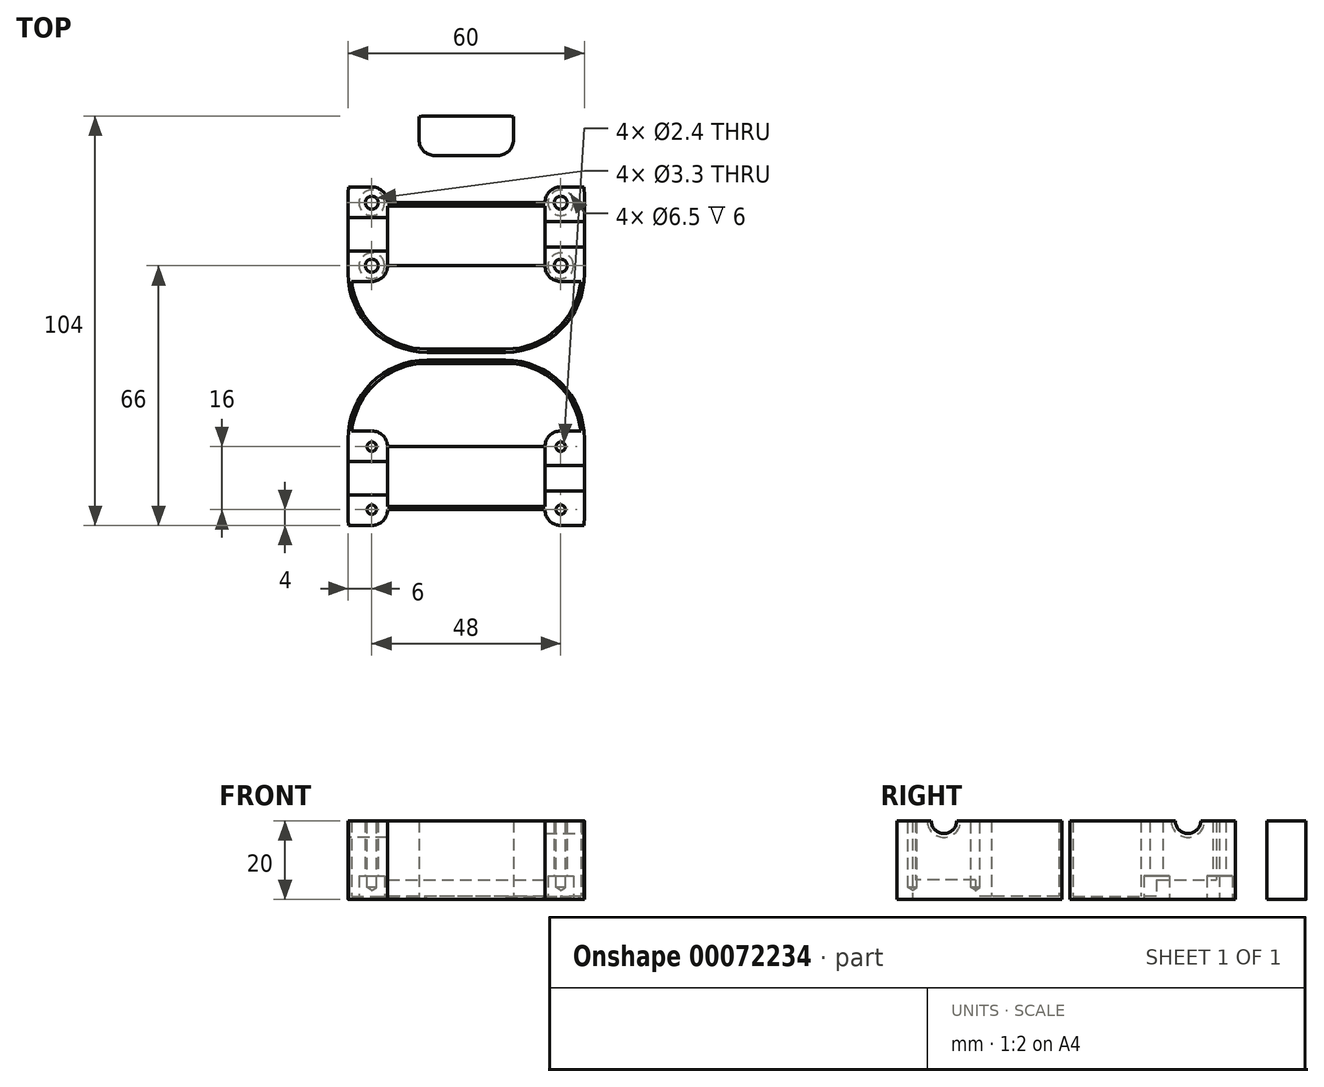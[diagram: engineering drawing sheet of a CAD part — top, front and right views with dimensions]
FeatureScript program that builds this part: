
annotation { "Feature Type Name" : "Feature", "Feature Type Description" : "" }
export const myFeature = defineFeature(function(context is Context, id is Id, definition is map)
    precondition{}
    {
        {
            var Q0;
            Q0=qCreatedBy(makeId("Top.planeOp"),FACE);
            var sketch = newSketch(context, id + "F0", { "sketchPlane" : qUnion([Q0])});
            skLineSegment(sketch, "E0", {"start": v(0, 0) * mm, "end": v(-30, 0) * mm, "construction": true});
            skLineSegment(sketch, "E1", {"start": v(0, 0) * mm, "end": v(0, 30) * mm, "construction": true});
            skLineSegment(sketch, "E2", {"start": v(0, 30) * mm, "end": v(-10, 30) * mm});
            skLineSegment(sketch, "E3", {"start": v(-30, 10) * mm, "end": v(-30, 0) * mm});
            skPoint(sketch, "E4.visualSharp", {"position": v(-30, 30) * mm});
            skArc(sketch, "E4.filletArc", {"start": v(-10, 30) * mm, "mid": v(-24.14, 24.14) * mm, "end": v(-30, 10) * mm});
            skArc(sketch, "E5.MirrorCS", {"start": v(10, 30) * mm, "mid": v(24.14, 24.14) * mm, "end": v(30, 10) * mm});
            skLineSegment(sketch, "E6.MirrorCS", {"start": v(30, 10) * mm, "end": v(30, 0) * mm});
            skLineSegment(sketch, "E7.MirrorCS", {"start": v(0, 30) * mm, "end": v(10, 30) * mm});
            skPoint(sketch, "E8.MirrorP", {"position": v(30, 30) * mm});
            skLineSegment(sketch, "E9.MirrorCS", {"start": v(0, -30) * mm, "end": v(-10, -30) * mm});
            skLineSegment(sketch, "E10.MirrorCS", {"start": v(-30, -10) * mm, "end": v(-30, 0) * mm});
            skLineSegment(sketch, "E11.MirrorCS", {"start": v(0, -30) * mm, "end": v(10, -30) * mm});
            skArc(sketch, "E12.MirrorCS", {"start": v(10, -30) * mm, "mid": v(24.14, -24.14) * mm, "end": v(30, -10) * mm});
            skArc(sketch, "E13.MirrorCS", {"start": v(-10, -30) * mm, "mid": v(-24.14, -24.14) * mm, "end": v(-30, -10) * mm});
            skLineSegment(sketch, "E14.MirrorCS", {"start": v(30, -10) * mm, "end": v(30, 0) * mm});
            skLineSegment(sketch, "E15.MirrorCS", {"start": v(0, 0) * mm, "end": v(0, -30) * mm, "construction": true});
            skPoint(sketch, "E16.MirrorP", {"position": v(30, -30) * mm});
            skPoint(sketch, "E17.MirrorP", {"position": v(-30, -30) * mm});
            skLineSegment(sketch, "E18", {"start": v(-16, 24) * mm, "end": v(0, 24) * mm, "construction": true});
            skLineSegment(sketch, "E19", {"start": v(-8, 30) * mm, "end": v(-8, 18.3) * mm, "construction": true});
            skPoint(sketch, "E19.startSnap0", {"position": v(-8, 24) * mm});
            skArc(sketch, "E20", {"start": v(-8, 20) * mm, "mid": v(-10.83, 21.17) * mm, "end": v(-12, 24) * mm});
            skLineSegment(sketch, "E21", {"start": v(-8, 20) * mm, "end": v(0, 20) * mm});
            skLineSegment(sketch, "E22", {"start": v(-24, 17.1) * mm, "end": v(-24, 0) * mm, "construction": true});
            skLineSegment(sketch, "E23", {"start": v(-30, 8) * mm, "end": v(-16.95, 8) * mm, "construction": true});
            skArc(sketch, "E24", {"start": v(-24, 12) * mm, "mid": v(-21.17, 10.83) * mm, "end": v(-20, 8) * mm});
            skLineSegment(sketch, "E25", {"start": v(-20, 8) * mm, "end": v(-20, 0) * mm});
            skLineSegment(sketch, "E26", {"start": v(-24, 12) * mm, "end": v(-36.57, 12) * mm});
            skLineSegment(sketch, "E27.MirrorCS", {"start": v(-24, -12) * mm, "end": v(-36.57, -12) * mm});
            skLineSegment(sketch, "E28.MirrorCS", {"start": v(-20, -8) * mm, "end": v(-20, 0) * mm});
            skArc(sketch, "E29.MirrorCS", {"start": v(-24, -12) * mm, "mid": v(-21.17, -10.83) * mm, "end": v(-20, -8) * mm});
            skLineSegment(sketch, "E30.MirrorCS", {"start": v(24, 12) * mm, "end": v(36.57, 12) * mm});
            skArc(sketch, "E31.MirrorCS", {"start": v(24, 12) * mm, "mid": v(21.17, 10.83) * mm, "end": v(20, 8) * mm});
            skLineSegment(sketch, "E32.MirrorCS", {"start": v(20, 8) * mm, "end": v(20, 0) * mm});
            skLineSegment(sketch, "E33.MirrorCS", {"start": v(24, -12) * mm, "end": v(36.57, -12) * mm});
            skLineSegment(sketch, "E34.MirrorCS", {"start": v(20, -8) * mm, "end": v(20, 0) * mm});
            skArc(sketch, "E35.MirrorCS", {"start": v(24, -12) * mm, "mid": v(21.17, -10.83) * mm, "end": v(20, -8) * mm});
            skLineSegment(sketch, "E36", {"start": v(-12, 24) * mm, "end": v(-12, 35.75) * mm});
            skLineSegment(sketch, "E37.MirrorCS", {"start": v(8, 20) * mm, "end": v(0, 20) * mm});
            skLineSegment(sketch, "E38.MirrorCS", {"start": v(12, 24) * mm, "end": v(12, 35.75) * mm});
            skArc(sketch, "E39.MirrorCS", {"start": v(8, 20) * mm, "mid": v(10.83, 21.17) * mm, "end": v(12, 24) * mm});
            skLineSegment(sketch, "E40.bottom", {"start": v(-20, -8) * mm, "end": v(20, -8) * mm});
            skLineSegment(sketch, "E40.top", {"start": v(-20, 8) * mm, "end": v(20, 8) * mm});
            skLineSegment(sketch, "E40.left", {"start": v(-20, -8) * mm, "end": v(-20, 8) * mm});
            skLineSegment(sketch, "E40.right", {"start": v(20, -8) * mm, "end": v(20, 8) * mm});
            skSolve(sketch);
        }
        {
            var Q0;
            {var subQ19=sQuery(id+"F0.wireOp",EDGE,"E9.MirrorCS");Q0=makeQuery(id+"F0.imprint","IMPRINT",FACE,{"disambiguationData":[TD([[makeQuery(id+"F0.imprint","IMPRINT",EDGE,{"derivedFrom":subQ19}),-1.0]])]});}
            var Q1;
            {var subQ6=sQuery(id+"F0.wireOp",EDGE,"E3");Q1=makeQuery(id+"F0.imprint","IMPRINT",FACE,{"disambiguationData":[TD([[makeQuery(id+"F0.imprint","IMPRINT",EDGE,{"derivedFrom":subQ6}),1.0]])]});}
            var Q2;
            {var subQ1=sQuery(id+"F0.wireOp",EDGE,"E6.MirrorCS");Q2=makeQuery(id+"F0.imprint","IMPRINT",FACE,{"disambiguationData":[TD([[makeQuery(id+"F0.imprint","IMPRINT",EDGE,{"derivedFrom":subQ1}),-1.0]])]});}
            var Q3;
            {var subQ1=sQuery(id+"F0.wireOp",EDGE,"E2");Q3=makeQuery(id+"F0.imprint","IMPRINT",FACE,{"disambiguationData":[TD([[makeQuery(id+"F0.imprint","IMPRINT",EDGE,{"derivedFrom":subQ1}),1.0]])]});}
            var Q4;
            {var subQ1=sQuery(id+"F0.wireOp",EDGE,"E20");Q4=makeQuery(id+"F0.imprint","IMPRINT",FACE,{"disambiguationData":[TD([[makeQuery(id+"F0.imprint","IMPRINT",EDGE,{"derivedFrom":subQ1}),1.0]])]});}
            var Q5;
            Q5=makeQuery(id+"F0.imprint","IMPRINT",FACE,{"disambiguationData":[TD([[makeQuery(id+"F0.imprint","IMPRINT",EDGE,{"derivedFrom":sQuery(id+"F0.wireOp",EDGE,"E40.bottom")}),1.0]])]});
            extrude(context, id + "F1", {"entities" : qUnion([Q0, Q1, Q2, Q3, Q4, Q5]), "depth" : 20 * mm, "offsetDistance" : 25 * mm});
        }
        {
            var Q0;
            Q0=makeQuery(id+"F1.opExtrude","CAP_FACE",FACE,{"disambiguationData":[OSD([sQuery(id+"F0.wireOp",EDGE,"E3"),sQuery(id+"F0.wireOp",EDGE,"E6.MirrorCS"),sQuery(id+"F0.wireOp",EDGE,"E4.filletArc"),sQuery(id+"F0.wireOp",EDGE,"E5.MirrorCS"),sQuery(id+"F0.wireOp",EDGE,"E2"),sQuery(id+"F0.wireOp",EDGE,"E7.MirrorCS"),sQuery(id+"F0.wireOp",EDGE,"E9.MirrorCS"),sQuery(id+"F0.wireOp",EDGE,"E12.MirrorCS"),sQuery(id+"F0.wireOp",EDGE,"E11.MirrorCS"),sQuery(id+"F0.wireOp",EDGE,"E10.MirrorCS"),sQuery(id+"F0.wireOp",EDGE,"E14.MirrorCS"),sQuery(id+"F0.wireOp",EDGE,"E13.MirrorCS")])],"isStart":false});
            shell(context, id + "F2", {"entities" : qUnion([Q0]), "thickness" : 0.8 * mm});
        }
        {
            var Q0;
            Q0=makeQuery(id+"F0.imprint","IMPRINT",FACE,{"disambiguationData":[TD([[makeQuery(id+"F0.imprint","IMPRINT",EDGE,{"derivedFrom":sQuery(id+"F0.wireOp",EDGE,"E40.bottom")}),1.0]])]});
            extrude(context, id + "F3", {"entities" : qUnion([Q0]), "operationType" : NewBodyOperationType.ADD, "depth" : 5 * mm, "offsetDistance" : 25 * mm});
        }
        {
            var Q0;
            {var subQ1=sQuery(id+"F0.wireOp",EDGE,"E14.MirrorCS");Q0=makeQuery(id+"F0.imprint","IMPRINT",FACE,{"disambiguationData":[TD([[makeQuery(id+"F0.imprint","IMPRINT",EDGE,{"derivedFrom":subQ1}),1.0]])]});}
            var Q1;
            {var subQ2=sQuery(id+"F0.wireOp",EDGE,"14543c69-8659-48dd-a31f-9fa6a3777b9e38.MirrorCS");Q1=makeQuery(id+"F0.imprint","IMPRINT",FACE,{"disambiguationData":[TD([[makeQuery(id+"F0.imprint","IMPRINT",EDGE,{"derivedFrom":subQ2}),-1.0]])]});}
            var Q2;
            Q2=makeQuery(id+"F0.imprint","IMPRINT",FACE,{"disambiguationData":[TD([[makeQuery(id+"F0.imprint","IMPRINT",EDGE,{"derivedFrom":sQuery(id+"F0.wireOp",EDGE,"E2")}),1.0]])]});
            var Q3;
            {var subQ3=sQuery(id+"F0.wireOp",EDGE,"E10.MirrorCS");Q3=makeQuery(id+"F0.imprint","IMPRINT",FACE,{"disambiguationData":[TD([[makeQuery(id+"F0.imprint","IMPRINT",EDGE,{"derivedFrom":subQ3}),-1.0]])]});}
            var Q4;
            {var subQ3=sQuery(id+"F0.wireOp",EDGE,"E3");Q4=makeQuery(id+"F0.imprint","IMPRINT",FACE,{"disambiguationData":[TD([[makeQuery(id+"F0.imprint","IMPRINT",EDGE,{"derivedFrom":subQ3}),1.0]])]});}
            var Q5;
            Q5=sQuery(id+"F0.wireOp",EDGE,"b274ORE4-UM5T-iyJz-Mf7x-KISBnKHlPYNR");
            extrude(context, id + "F4", {"entities" : qUnion([Q0, Q1, Q2, Q3, Q4]), "operationType" : NewBodyOperationType.ADD, "surfaceEntities" : qUnion([Q5]), "depth" : 20 * mm});
        }
        {
            var Q0;
            Q0=makeQuery(id+"F1.opExtrude","SWEPT_FACE",FACE,{"disambiguationData":[OSD([sQuery(id+"F0.wireOp",EDGE,"E3"),sQuery(id+"F0.wireOp",EDGE,"E10.MirrorCS"),sQuery(id+"F0.wireOp",EDGE,"e1145777-d645-4c14-8510-543826b77d7c3.MirrorCS"),sQuery(id+"F0.wireOp",EDGE,"e1145777-d645-4c14-8510-543826b77d7c7.MirrorCS")])]});
            var sketch = newSketch(context, id + "F5", { "sketchPlane" : qUnion([Q0])});
            skPoint(sketch, "E41", {"position": v(0, 20) * mm});
            skSolve(sketch);
        }
        {
            var Q0;
            Q0=sQuery(id+"F5.wireOp",VERTEX,"E41");
            var Q1;
            Q1=makeQuery(id+"F1.opExtrude","SWEPT_BODY",BODY,{"disambiguationData":[OSD([sQuery(id+"F0.wireOp",EDGE,"E3"),sQuery(id+"F0.wireOp",EDGE,"E6.MirrorCS"),sQuery(id+"F0.wireOp",EDGE,"E4.filletArc"),sQuery(id+"F0.wireOp",EDGE,"E5.MirrorCS"),sQuery(id+"F0.wireOp",EDGE,"E2"),sQuery(id+"F0.wireOp",EDGE,"E7.MirrorCS"),sQuery(id+"F0.wireOp",EDGE,"E9.MirrorCS"),sQuery(id+"F0.wireOp",EDGE,"E12.MirrorCS"),sQuery(id+"F0.wireOp",EDGE,"E11.MirrorCS"),sQuery(id+"F0.wireOp",EDGE,"E10.MirrorCS"),sQuery(id+"F0.wireOp",EDGE,"E14.MirrorCS"),sQuery(id+"F0.wireOp",EDGE,"E13.MirrorCS"),sQuery(id+"F0.wireOp",EDGE,"b274ORE4-UM5T-iyJz-Mf7x-KISBnKHlPYNR"),sQuery(id+"F0.wireOp",EDGE,"e1145777-d645-4c14-8510-543826b77d7c3.MirrorCS"),sQuery(id+"F0.wireOp",EDGE,"e1145777-d645-4c14-8510-543826b77d7c7.MirrorCS"),sQuery(id+"F0.wireOp",EDGE,"d4da72d8-b042-4007-9413-fc62ccedf90810.MirrorCS"),sQuery(id+"F0.wireOp",EDGE,"d4da72d8-b042-4007-9413-fc62ccedf90813.MirrorCS"),sQuery(id+"F0.wireOp",EDGE,"A0MarJfp-02qR-F9tc-DTzI-DnbxqoHxPLbg.bottom"),sQuery(id+"F0.wireOp",EDGE,"92cf4c97-c3a1-482c-a76c-706df4ada76c3.MirrorCS")])]});
            var Q2;
            Q2=makeQuery(id+"FBtsKpCSnu7iRzL_1.opExtrude","SWEPT_BODY",BODY,{"disambiguationData":[OSD([sQuery(id+"F0.wireOp",EDGE,"E3"),sQuery(id+"F0.wireOp",EDGE,"E6.MirrorCS"),sQuery(id+"F0.wireOp",EDGE,"E4.filletArc"),sQuery(id+"F0.wireOp",EDGE,"E5.MirrorCS"),sQuery(id+"F0.wireOp",EDGE,"E2"),sQuery(id+"F0.wireOp",EDGE,"E7.MirrorCS"),sQuery(id+"F0.wireOp",EDGE,"E9.MirrorCS"),sQuery(id+"F0.wireOp",EDGE,"E12.MirrorCS"),sQuery(id+"F0.wireOp",EDGE,"E11.MirrorCS"),sQuery(id+"F0.wireOp",EDGE,"E10.MirrorCS"),sQuery(id+"F0.wireOp",EDGE,"E14.MirrorCS"),sQuery(id+"F0.wireOp",EDGE,"E13.MirrorCS"),sQuery(id+"F0.wireOp",EDGE,"b274ORE4-UM5T-iyJz-Mf7x-KISBnKHlPYNR"),sQuery(id+"F0.wireOp",EDGE,"e1145777-d645-4c14-8510-543826b77d7c3.MirrorCS"),sQuery(id+"F0.wireOp",EDGE,"e1145777-d645-4c14-8510-543826b77d7c7.MirrorCS"),sQuery(id+"F0.wireOp",EDGE,"d4da72d8-b042-4007-9413-fc62ccedf90810.MirrorCS"),sQuery(id+"F0.wireOp",EDGE,"d4da72d8-b042-4007-9413-fc62ccedf90813.MirrorCS"),sQuery(id+"F0.wireOp",EDGE,"A0MarJfp-02qR-F9tc-DTzI-DnbxqoHxPLbg.bottom"),sQuery(id+"F0.wireOp",EDGE,"92cf4c97-c3a1-482c-a76c-706df4ada76c3.MirrorCS")])]});
            hole(context, id + "F6", {"style" : HoleStyle.SIMPLE, "endStyle" : HoleEndStyle.BLIND, "holeDiameter" : 8.5 * mm, "holeDepth" : 12 * mm, "locations" : qUnion([Q0]), "scope" : qUnion([Q1, Q2])});
        }
        {
            var Q0;
            Q0=makeQuery(id+"F1.opExtrude","SWEPT_FACE",FACE,{"disambiguationData":[OSD([sQuery(id+"F0.wireOp",EDGE,"E2"),sQuery(id+"F0.wireOp",EDGE,"E7.MirrorCS"),sQuery(id+"F0.wireOp",EDGE,"A0MarJfp-02qR-F9tc-DTzI-DnbxqoHxPLbg.bottom"),sQuery(id+"F0.wireOp",EDGE,"92cf4c97-c3a1-482c-a76c-706df4ada76c3.MirrorCS")])]});
            var sketch = newSketch(context, id + "F7", { "sketchPlane" : qUnion([Q0])});
            skPoint(sketch, "E42", {"position": v(0, 20) * mm});
            skSolve(sketch);
        }
        {
            var Q0;
            Q0=sQuery(id+"F7.wireOp",VERTEX,"E42");
            var Q1;
            Q1=makeQuery(id+"F1.opExtrude","SWEPT_BODY",BODY,{"disambiguationData":[OSD([sQuery(id+"F0.wireOp",EDGE,"E3"),sQuery(id+"F0.wireOp",EDGE,"E6.MirrorCS"),sQuery(id+"F0.wireOp",EDGE,"E4.filletArc"),sQuery(id+"F0.wireOp",EDGE,"E5.MirrorCS"),sQuery(id+"F0.wireOp",EDGE,"E2"),sQuery(id+"F0.wireOp",EDGE,"E7.MirrorCS"),sQuery(id+"F0.wireOp",EDGE,"E9.MirrorCS"),sQuery(id+"F0.wireOp",EDGE,"E12.MirrorCS"),sQuery(id+"F0.wireOp",EDGE,"E11.MirrorCS"),sQuery(id+"F0.wireOp",EDGE,"E10.MirrorCS"),sQuery(id+"F0.wireOp",EDGE,"E14.MirrorCS"),sQuery(id+"F0.wireOp",EDGE,"E13.MirrorCS"),sQuery(id+"F0.wireOp",EDGE,"b274ORE4-UM5T-iyJz-Mf7x-KISBnKHlPYNR"),sQuery(id+"F0.wireOp",EDGE,"e1145777-d645-4c14-8510-543826b77d7c3.MirrorCS"),sQuery(id+"F0.wireOp",EDGE,"e1145777-d645-4c14-8510-543826b77d7c7.MirrorCS"),sQuery(id+"F0.wireOp",EDGE,"d4da72d8-b042-4007-9413-fc62ccedf90810.MirrorCS"),sQuery(id+"F0.wireOp",EDGE,"d4da72d8-b042-4007-9413-fc62ccedf90813.MirrorCS"),sQuery(id+"F0.wireOp",EDGE,"A0MarJfp-02qR-F9tc-DTzI-DnbxqoHxPLbg.bottom"),sQuery(id+"F0.wireOp",EDGE,"92cf4c97-c3a1-482c-a76c-706df4ada76c3.MirrorCS")])]});
            hole(context, id + "F8", {"style" : HoleStyle.SIMPLE, "endStyle" : HoleEndStyle.BLIND, "holeDiameter" : 8.5 * mm, "holeDepth" : 12 * mm, "locations" : qUnion([Q0]), "scope" : qUnion([Q1])});
        }
        {
            var Q0;
            Q0=makeQuery(id+"F1.opExtrude","SWEPT_FACE",FACE,{"disambiguationData":[OSD([sQuery(id+"F0.wireOp",EDGE,"E6.MirrorCS"),sQuery(id+"F0.wireOp",EDGE,"E14.MirrorCS")])]});
            var sketch = newSketch(context, id + "F9", { "sketchPlane" : qUnion([Q0])});
            skPoint(sketch, "E43", {"position": v(0, 20) * mm});
            skSolve(sketch);
        }
        {
            var Q0;
            Q0=sQuery(id+"F9.wireOp",VERTEX,"E43");
            var Q1;
            Q1=makeQuery(id+"F1.opExtrude","SWEPT_BODY",BODY,{"disambiguationData":[OSD([sQuery(id+"F0.wireOp",EDGE,"E3"),sQuery(id+"F0.wireOp",EDGE,"E6.MirrorCS"),sQuery(id+"F0.wireOp",EDGE,"E4.filletArc"),sQuery(id+"F0.wireOp",EDGE,"E5.MirrorCS"),sQuery(id+"F0.wireOp",EDGE,"E2"),sQuery(id+"F0.wireOp",EDGE,"E7.MirrorCS"),sQuery(id+"F0.wireOp",EDGE,"E9.MirrorCS"),sQuery(id+"F0.wireOp",EDGE,"E12.MirrorCS"),sQuery(id+"F0.wireOp",EDGE,"E11.MirrorCS"),sQuery(id+"F0.wireOp",EDGE,"E10.MirrorCS"),sQuery(id+"F0.wireOp",EDGE,"E14.MirrorCS"),sQuery(id+"F0.wireOp",EDGE,"E13.MirrorCS"),sQuery(id+"F0.wireOp",EDGE,"b274ORE4-UM5T-iyJz-Mf7x-KISBnKHlPYNR"),sQuery(id+"F0.wireOp",EDGE,"e1145777-d645-4c14-8510-543826b77d7c3.MirrorCS"),sQuery(id+"F0.wireOp",EDGE,"e1145777-d645-4c14-8510-543826b77d7c7.MirrorCS"),sQuery(id+"F0.wireOp",EDGE,"d4da72d8-b042-4007-9413-fc62ccedf90810.MirrorCS"),sQuery(id+"F0.wireOp",EDGE,"d4da72d8-b042-4007-9413-fc62ccedf90813.MirrorCS"),sQuery(id+"F0.wireOp",EDGE,"A0MarJfp-02qR-F9tc-DTzI-DnbxqoHxPLbg.bottom"),sQuery(id+"F0.wireOp",EDGE,"92cf4c97-c3a1-482c-a76c-706df4ada76c3.MirrorCS")])]});
            var Q2;
            Q2=makeQuery(id+"FBtsKpCSnu7iRzL_1.opExtrude","SWEPT_BODY",BODY,{"disambiguationData":[OSD([sQuery(id+"F0.wireOp",EDGE,"E3"),sQuery(id+"F0.wireOp",EDGE,"E6.MirrorCS"),sQuery(id+"F0.wireOp",EDGE,"E4.filletArc"),sQuery(id+"F0.wireOp",EDGE,"E5.MirrorCS"),sQuery(id+"F0.wireOp",EDGE,"E2"),sQuery(id+"F0.wireOp",EDGE,"E7.MirrorCS"),sQuery(id+"F0.wireOp",EDGE,"E9.MirrorCS"),sQuery(id+"F0.wireOp",EDGE,"E12.MirrorCS"),sQuery(id+"F0.wireOp",EDGE,"E11.MirrorCS"),sQuery(id+"F0.wireOp",EDGE,"E10.MirrorCS"),sQuery(id+"F0.wireOp",EDGE,"E14.MirrorCS"),sQuery(id+"F0.wireOp",EDGE,"E13.MirrorCS"),sQuery(id+"F0.wireOp",EDGE,"b274ORE4-UM5T-iyJz-Mf7x-KISBnKHlPYNR"),sQuery(id+"F0.wireOp",EDGE,"e1145777-d645-4c14-8510-543826b77d7c3.MirrorCS"),sQuery(id+"F0.wireOp",EDGE,"e1145777-d645-4c14-8510-543826b77d7c7.MirrorCS"),sQuery(id+"F0.wireOp",EDGE,"d4da72d8-b042-4007-9413-fc62ccedf90810.MirrorCS"),sQuery(id+"F0.wireOp",EDGE,"d4da72d8-b042-4007-9413-fc62ccedf90813.MirrorCS"),sQuery(id+"F0.wireOp",EDGE,"A0MarJfp-02qR-F9tc-DTzI-DnbxqoHxPLbg.bottom"),sQuery(id+"F0.wireOp",EDGE,"92cf4c97-c3a1-482c-a76c-706df4ada76c3.MirrorCS")])]});
            hole(context, id + "F10", {"style" : HoleStyle.SIMPLE, "endStyle" : HoleEndStyle.BLIND, "holeDiameter" : 6.5 * mm, "holeDepth" : 12 * mm, "locations" : qUnion([Q0]), "scope" : qUnion([Q1, Q2])});
        }
        {
            var Q0;
            Q0=qCreatedBy(makeId("Front.planeOp"),FACE);
            cPlane(context, id + "F11", {"entities" : qUnion([Q0]), "cplaneType" : CPlaneType.OFFSET, "offset" : 31 * mm, "width" : 150 * mm, "height" : 150 * mm});
        }
        {
            var Q0;
            Q0=makeQuery(id+"F1.opExtrude","SWEPT_BODY",BODY,{"disambiguationData":[OSD([sQuery(id+"F0.wireOp",EDGE,"E3"),sQuery(id+"F0.wireOp",EDGE,"E6.MirrorCS"),sQuery(id+"F0.wireOp",EDGE,"E4.filletArc"),sQuery(id+"F0.wireOp",EDGE,"E5.MirrorCS"),sQuery(id+"F0.wireOp",EDGE,"E2"),sQuery(id+"F0.wireOp",EDGE,"E7.MirrorCS"),sQuery(id+"F0.wireOp",EDGE,"E9.MirrorCS"),sQuery(id+"F0.wireOp",EDGE,"E12.MirrorCS"),sQuery(id+"F0.wireOp",EDGE,"E11.MirrorCS"),sQuery(id+"F0.wireOp",EDGE,"E10.MirrorCS"),sQuery(id+"F0.wireOp",EDGE,"E14.MirrorCS"),sQuery(id+"F0.wireOp",EDGE,"E13.MirrorCS"),sQuery(id+"F0.wireOp",EDGE,"b274ORE4-UM5T-iyJz-Mf7x-KISBnKHlPYNR"),sQuery(id+"F0.wireOp",EDGE,"e1145777-d645-4c14-8510-543826b77d7c3.MirrorCS"),sQuery(id+"F0.wireOp",EDGE,"e1145777-d645-4c14-8510-543826b77d7c7.MirrorCS"),sQuery(id+"F0.wireOp",EDGE,"d4da72d8-b042-4007-9413-fc62ccedf90810.MirrorCS"),sQuery(id+"F0.wireOp",EDGE,"d4da72d8-b042-4007-9413-fc62ccedf90813.MirrorCS"),sQuery(id+"F0.wireOp",EDGE,"A0MarJfp-02qR-F9tc-DTzI-DnbxqoHxPLbg.bottom"),sQuery(id+"F0.wireOp",EDGE,"92cf4c97-c3a1-482c-a76c-706df4ada76c3.MirrorCS")])]});
            var Q1;
            Q1=qCreatedBy(id+"F11.planeOp",FACE);
            mirror(context, id + "F12", {"entities" : qUnion([Q0]), "mirrorPlane" : qUnion([Q1])});
        }
        {
            var Q0;
            Q0=sQuery(id+"F0.wireOp",VERTEX,"E24.center");
            var Q1;
            Q1=sQuery(id+"F0.wireOp",VERTEX,"E31.MirrorCS.center");
            var Q2;
            Q2=sQuery(id+"F0.wireOp",VERTEX,"E35.MirrorCS.center");
            var Q3;
            Q3=sQuery(id+"F0.wireOp",VERTEX,"E29.MirrorCS.center");
            var Q4;
            Q4=makeQuery(id+"F1.opExtrude","SWEPT_BODY",BODY,{"disambiguationData":[OSD([sQuery(id+"F0.wireOp",EDGE,"E3"),sQuery(id+"F0.wireOp",EDGE,"E6.MirrorCS"),sQuery(id+"F0.wireOp",EDGE,"E4.filletArc"),sQuery(id+"F0.wireOp",EDGE,"E5.MirrorCS"),sQuery(id+"F0.wireOp",EDGE,"E2"),sQuery(id+"F0.wireOp",EDGE,"E7.MirrorCS"),sQuery(id+"F0.wireOp",EDGE,"E9.MirrorCS"),sQuery(id+"F0.wireOp",EDGE,"E12.MirrorCS"),sQuery(id+"F0.wireOp",EDGE,"E11.MirrorCS"),sQuery(id+"F0.wireOp",EDGE,"E10.MirrorCS"),sQuery(id+"F0.wireOp",EDGE,"E14.MirrorCS"),sQuery(id+"F0.wireOp",EDGE,"E13.MirrorCS"),sQuery(id+"F0.wireOp",EDGE,"b274ORE4-UM5T-iyJz-Mf7x-KISBnKHlPYNR"),sQuery(id+"F0.wireOp",EDGE,"e1145777-d645-4c14-8510-543826b77d7c3.MirrorCS"),sQuery(id+"F0.wireOp",EDGE,"e1145777-d645-4c14-8510-543826b77d7c7.MirrorCS"),sQuery(id+"F0.wireOp",EDGE,"d4da72d8-b042-4007-9413-fc62ccedf90810.MirrorCS"),sQuery(id+"F0.wireOp",EDGE,"d4da72d8-b042-4007-9413-fc62ccedf90813.MirrorCS"),sQuery(id+"F0.wireOp",EDGE,"A0MarJfp-02qR-F9tc-DTzI-DnbxqoHxPLbg.bottom"),sQuery(id+"F0.wireOp",EDGE,"92cf4c97-c3a1-482c-a76c-706df4ada76c3.MirrorCS")])]});
            var Q5;
            Q5=makeQuery(id+"F12.opPattern","COPY",BODY,{"derivedFrom":makeQuery(id+"F1.opExtrude","SWEPT_BODY",BODY,{"disambiguationData":[OSD([sQuery(id+"F0.wireOp",EDGE,"E3"),sQuery(id+"F0.wireOp",EDGE,"E6.MirrorCS"),sQuery(id+"F0.wireOp",EDGE,"E4.filletArc"),sQuery(id+"F0.wireOp",EDGE,"E5.MirrorCS"),sQuery(id+"F0.wireOp",EDGE,"E2"),sQuery(id+"F0.wireOp",EDGE,"E7.MirrorCS"),sQuery(id+"F0.wireOp",EDGE,"E9.MirrorCS"),sQuery(id+"F0.wireOp",EDGE,"E12.MirrorCS"),sQuery(id+"F0.wireOp",EDGE,"E11.MirrorCS"),sQuery(id+"F0.wireOp",EDGE,"E10.MirrorCS"),sQuery(id+"F0.wireOp",EDGE,"E14.MirrorCS"),sQuery(id+"F0.wireOp",EDGE,"E13.MirrorCS"),sQuery(id+"F0.wireOp",EDGE,"b274ORE4-UM5T-iyJz-Mf7x-KISBnKHlPYNR"),sQuery(id+"F0.wireOp",EDGE,"e1145777-d645-4c14-8510-543826b77d7c3.MirrorCS"),sQuery(id+"F0.wireOp",EDGE,"e1145777-d645-4c14-8510-543826b77d7c7.MirrorCS"),sQuery(id+"F0.wireOp",EDGE,"d4da72d8-b042-4007-9413-fc62ccedf90810.MirrorCS"),sQuery(id+"F0.wireOp",EDGE,"d4da72d8-b042-4007-9413-fc62ccedf90813.MirrorCS"),sQuery(id+"F0.wireOp",EDGE,"A0MarJfp-02qR-F9tc-DTzI-DnbxqoHxPLbg.bottom"),sQuery(id+"F0.wireOp",EDGE,"92cf4c97-c3a1-482c-a76c-706df4ada76c3.MirrorCS")])]}),"instanceName":"1"});
            hole(context, id + "F13", {"style" : HoleStyle.C_BORE, "endStyle" : HoleEndStyle.THROUGH, "oppositeDirection" : true, "holeDiameter" : 3.3 * mm, "cBoreDiameter" : 6.5 * mm, "cBoreDepth" : 6 * mm, "locations" : qUnion([Q0, Q1, Q2, Q3]), "scope" : qUnion([Q4, Q5]), "isTappedThrough" : true});
        }
        {
            var Q0;
            {var subQ0=sQuery(id+"F0.wireOp",EDGE,"E26");var subQ1=sQuery(id+"F0.wireOp",EDGE,"E28.MirrorCS");var subQ2=sQuery(id+"F0.wireOp",EDGE,"E25");var subQ3=sQuery(id+"F0.wireOp",EDGE,"E10.MirrorCS");var subQ4=sQuery(id+"F0.wireOp",EDGE,"E3");var subQ5=sQuery(id+"F0.wireOp",EDGE,"E24");var subQ6=sQuery(id+"F0.wireOp",EDGE,"E37.MirrorCS");var subQ7=sQuery(id+"F0.wireOp",EDGE,"E21");var subQ8=sQuery(id+"F0.wireOp",EDGE,"E20");var subQ9=sQuery(id+"F0.wireOp",EDGE,"E4.filletArc");var subQ10=sQuery(id+"F0.wireOp",EDGE,"E36");var subQ11=sQuery(id+"F0.wireOp",EDGE,"E7.MirrorCS");var subQ12=sQuery(id+"F0.wireOp",EDGE,"E2");var subQ13=sQuery(id+"F0.wireOp",EDGE,"E14.MirrorCS");var subQ14=sQuery(id+"F0.wireOp",EDGE,"E6.MirrorCS");var subQ15=sQuery(id+"F0.wireOp",EDGE,"E12.MirrorCS");var subQ16=sQuery(id+"F0.wireOp",EDGE,"E5.MirrorCS");var subQ17=sQuery(id+"F0.wireOp",EDGE,"E13.MirrorCS");Q0=makeQuery(id+"F12.opPattern","COPY",FACE,{"derivedFrom":makeQuery(id+"F8.hole-0.boolean.opBoolean","SPLIT",FACE,{"disambiguationData":[TD([makeQuery(id+"F1.opExtrude","SWEPT_FACE",FACE,{"disambiguationData":[OSD([subQ9])]})])],"derivedFrom":makeQuery(id+"F4.boolean.opBoolean","MERGE",FACE,{"derivedFrom":[makeQuery(id+"F1.opExtrude","CAP_FACE",FACE,{"disambiguationData":[OSD([subQ4,subQ9,subQ16,subQ12,subQ11,sQuery(id+"F0.wireOp",EDGE,"E9.MirrorCS"),subQ15,sQuery(id+"F0.wireOp",EDGE,"E11.MirrorCS"),subQ3,subQ17,subQ14,subQ13])],"isStart":false}),makeQuery(id+"F4.opExtrude","CAP_FACE",FACE,{"disambiguationData":[OSD([subQ4,subQ9,subQ3,subQ17,subQ5,subQ2,sQuery(id+"F0.wireOp",EDGE,"E27.MirrorCS"),subQ1,sQuery(id+"F0.wireOp",EDGE,"E29.MirrorCS"),subQ0])],"isStart":false}),makeQuery(id+"F4.opExtrude","CAP_FACE",FACE,{"disambiguationData":[OSD([subQ9,subQ16,subQ12,subQ11,subQ8,subQ7,subQ10,subQ6,sQuery(id+"F0.wireOp",EDGE,"E38.MirrorCS"),sQuery(id+"F0.wireOp",EDGE,"E39.MirrorCS")])],"isStart":false}),makeQuery(id+"F4.opExtrude","CAP_FACE",FACE,{"disambiguationData":[OSD([subQ16,subQ15,subQ14,subQ13,sQuery(id+"F0.wireOp",EDGE,"E30.MirrorCS"),sQuery(id+"F0.wireOp",EDGE,"E31.MirrorCS"),sQuery(id+"F0.wireOp",EDGE,"E32.MirrorCS"),sQuery(id+"F0.wireOp",EDGE,"E33.MirrorCS"),sQuery(id+"F0.wireOp",EDGE,"E34.MirrorCS"),sQuery(id+"F0.wireOp",EDGE,"E35.MirrorCS")])],"isStart":false})]})}),"instanceName":"1"});}
            var sketch = newSketch(context, id + "F14", { "sketchPlane" : qUnion([Q0])});
            skPoint(sketch, "E44", {"position": v(-24, -54) * mm});
            skPoint(sketch, "E45", {"position": v(24, -54) * mm});
            skPoint(sketch, "E46", {"position": v(24, -70) * mm});
            skPoint(sketch, "E47", {"position": v(-24, -70) * mm});
            skSolve(sketch);
        }
        {
            var Q0;
            Q0=sQuery(id+"F14.wireOp",VERTEX,"E44");
            var Q1;
            Q1=sQuery(id+"F14.wireOp",VERTEX,"E47");
            var Q2;
            Q2=sQuery(id+"F14.wireOp",VERTEX,"E46");
            var Q3;
            Q3=sQuery(id+"F14.wireOp",VERTEX,"E45");
            var Q4;
            Q4=makeQuery(id+"F12.opPattern","COPY",BODY,{"derivedFrom":makeQuery(id+"F1.opExtrude","SWEPT_BODY",BODY,{"disambiguationData":[OSD([sQuery(id+"F0.wireOp",EDGE,"E3"),sQuery(id+"F0.wireOp",EDGE,"E6.MirrorCS"),sQuery(id+"F0.wireOp",EDGE,"E4.filletArc"),sQuery(id+"F0.wireOp",EDGE,"E5.MirrorCS"),sQuery(id+"F0.wireOp",EDGE,"E2"),sQuery(id+"F0.wireOp",EDGE,"E7.MirrorCS"),sQuery(id+"F0.wireOp",EDGE,"E9.MirrorCS"),sQuery(id+"F0.wireOp",EDGE,"E12.MirrorCS"),sQuery(id+"F0.wireOp",EDGE,"E11.MirrorCS"),sQuery(id+"F0.wireOp",EDGE,"E10.MirrorCS"),sQuery(id+"F0.wireOp",EDGE,"E14.MirrorCS"),sQuery(id+"F0.wireOp",EDGE,"E13.MirrorCS"),sQuery(id+"F0.wireOp",EDGE,"b274ORE4-UM5T-iyJz-Mf7x-KISBnKHlPYNR"),sQuery(id+"F0.wireOp",EDGE,"e1145777-d645-4c14-8510-543826b77d7c3.MirrorCS"),sQuery(id+"F0.wireOp",EDGE,"e1145777-d645-4c14-8510-543826b77d7c7.MirrorCS"),sQuery(id+"F0.wireOp",EDGE,"d4da72d8-b042-4007-9413-fc62ccedf90810.MirrorCS"),sQuery(id+"F0.wireOp",EDGE,"d4da72d8-b042-4007-9413-fc62ccedf90813.MirrorCS"),sQuery(id+"F0.wireOp",EDGE,"A0MarJfp-02qR-F9tc-DTzI-DnbxqoHxPLbg.bottom"),sQuery(id+"F0.wireOp",EDGE,"92cf4c97-c3a1-482c-a76c-706df4ada76c3.MirrorCS")])]}),"instanceName":"1"});
            hole(context, id + "F15", {"style" : HoleStyle.SIMPLE, "endStyle" : HoleEndStyle.BLIND, "standardTappedOrClearance" : lookupTablePath({ "standard" : "ISO", "engagement" : "75%", "pitch" : "0.6 mm", "size" : "M3", "type" : "Tapped" }), "standardBlindInLast" : lookupTablePath({ "standard" : "ISO", "engagement" : "75%", "pitch" : "0.6 mm", "size" : "M3", "type" : "Tapped" }), "holeDiameter" : 2.4 * mm, "holeDepth" : 17 * mm, "locations" : qUnion([Q0, Q1, Q2, Q3]), "scope" : qUnion([Q4])});
        }
    });
